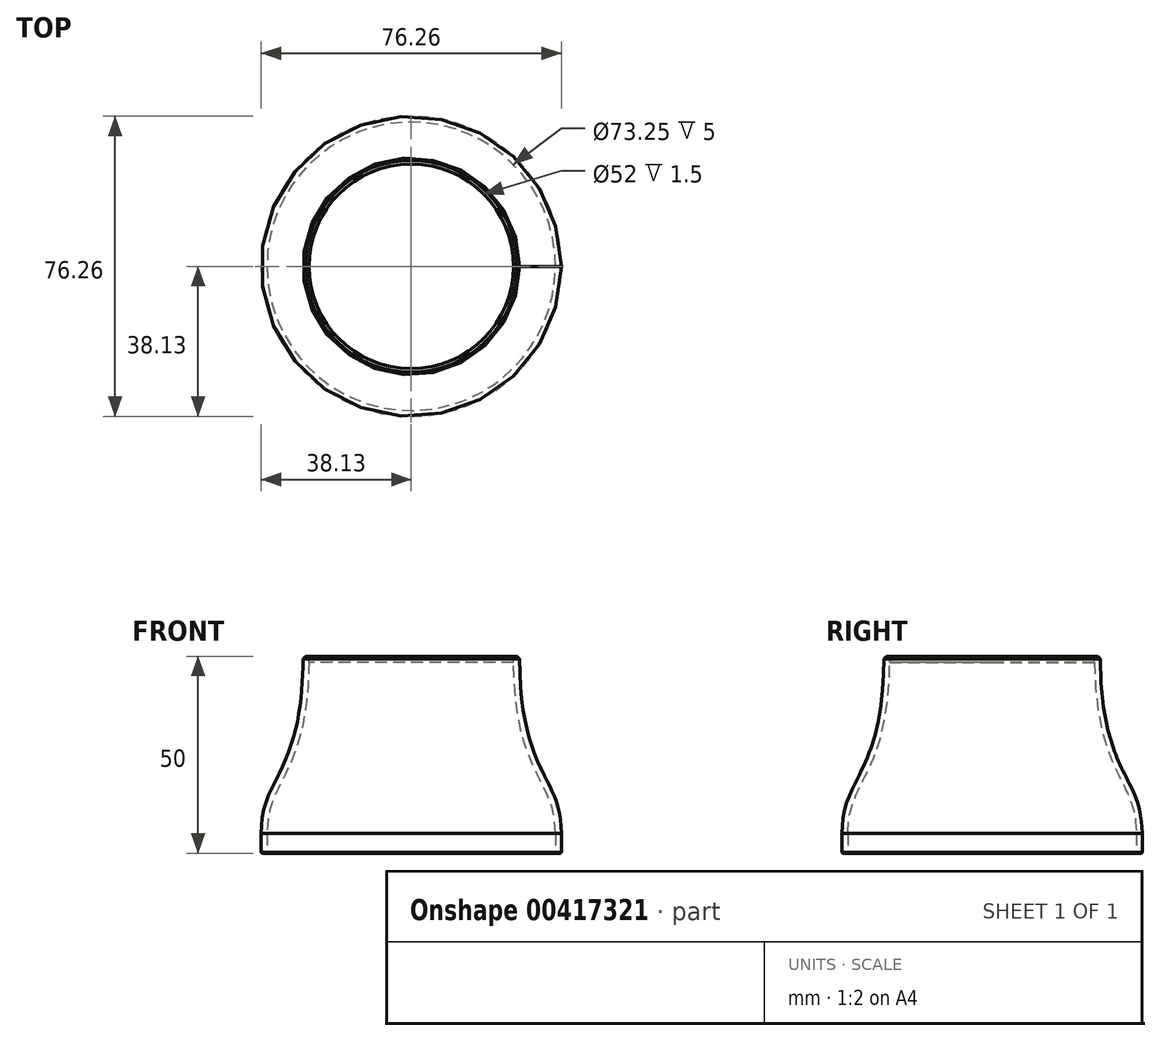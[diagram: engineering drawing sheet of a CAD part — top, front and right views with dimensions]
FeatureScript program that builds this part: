
annotation { "Feature Type Name" : "Feature", "Feature Type Description" : "" }
export const myFeature = defineFeature(function(context is Context, id is Id, definition is map)
    precondition{}
    {
        {
            var Q0;
            Q0=qCreatedBy(makeId("Top.planeOp"),FACE);
            var sketch = newSketch(context, id + "F0", { "sketchPlane" : qUnion([Q0])});
            skCircle(sketch, "E0", {"center": v(0, 0) * mm, "radius": 38.12 * mm});
            skSolve(sketch);
        }
        {
            var Q0;
            Q0 = qSketchRegion(id + "F0", true);
            extrude(context, id + "F1", {"entities" : qUnion([Q0]), "depth" : 5 * mm});
        }
        {
            var Q0;
            Q0=qCreatedBy(makeId("Top.planeOp"),FACE);
            cPlane(context, id + "F2", {"entities" : qUnion([Q0]), "cplaneType" : CPlaneType.OFFSET, "offset" : 50 * mm, "width" : 150 * mm, "height" : 150 * mm});
        }
        {
            var Q0;
            Q0=qCreatedBy(id+"F2.planeOp",FACE);
            var sketch = newSketch(context, id + "F3", { "sketchPlane" : qUnion([Q0])});
            skCircle(sketch, "E1", {"center": v(0, 0) * mm, "radius": 27.5 * mm});
            skSolve(sketch);
        }
        {
            var Q1;
            Q1=makeQuery(id+"F1.opExtrude","CAP_FACE",FACE,{"disambiguationData":[OSD([sQuery(id+"F0.wireOp",EDGE,"E0")])],"isStart":false});
            var Q2;
            Q2=makeQuery(id+"F3.imprint","IMPRINT",FACE,{"disambiguationData":[TD([[makeQuery(id+"F3.imprint","IMPRINT",EDGE,{"derivedFrom":sQuery(id+"F3.wireOp",EDGE,"E1")}),1.0]])]});
            loft(context, id + "F4", {"operationType" : NewBodyOperationType.ADD, "startCondition" : LoftEndDerivativeType.NORMAL_TO_PROFILE, "startMagnitude" : 1, "endCondition" : LoftEndDerivativeType.NORMAL_TO_PROFILE, "endMagnitude" : 2, "sheetProfilesArray" : [{ "sheetProfileEntities" : qUnion([Q1]) }, { "sheetProfileEntities" : qUnion([Q2]) }]});
        }
        {
            var Q0;
            Q0=makeQuery(id+"F1.opExtrude","CAP_FACE",FACE,{"disambiguationData":[OSD([sQuery(id+"F0.wireOp",EDGE,"E0")])],"isStart":true});
            shell(context, id + "F5", {"entities" : qUnion([Q0]), "thickness" : 1.5 * mm});
        }
        {
            var Q0;
            Q0=makeQuery(id+"F4.opLoft","CAP_FACE",FACE,{"disambiguationData":[OSD([makeQuery(id+"F3.imprint","IMPRINT",FACE,{"disambiguationData":[TD([[makeQuery(id+"F3.imprint","IMPRINT",EDGE,{"derivedFrom":sQuery(id+"F3.wireOp",EDGE,"E1")}),1.0]])]})])],"isStart":true});
            var sketch = newSketch(context, id + "F6", { "sketchPlane" : qUnion([Q0])});
            skCircle(sketch, "E2", {"center": v(0, 0) * mm, "radius": 26 * mm});
            skSolve(sketch);
        }
        {
            var Q0;
            Q0 = qSketchRegion(id + "F6", true);
            extrude(context, id + "F7", {"entities" : qUnion([Q0]), "operationType" : NewBodyOperationType.REMOVE, "oppositeDirection" : true, "depth" : 25 * mm});
        }
        {
            var Q0;
            Q0=makeQuery(id+"F4.opLoft","MID_CAP_EDGE",EDGE,{"disambiguationData":[OSD([sQuery(id+"F0.wireOp",EDGE,"E0"),sQuery(id+"F3.wireOp",EDGE,"E1")])],"capPos":1.0});
            chamfer(context, id + "F8", {"entities" : qUnion([Q0]), "width" : .6 * mm, "tangentPropagation" : true});
        }
        {
            var Q0;
            Q0=makeQuery(id+"F1.opExtrude","CAP_EDGE",EDGE,{"disambiguationData":[OSD([sQuery(id+"F0.wireOp",EDGE,"E0")])],"isStart":true});
            chamfer(context, id + "F9", {"entities" : qUnion([Q0]), "width" : .2 * mm, "tangentPropagation" : true});
        }
    });
